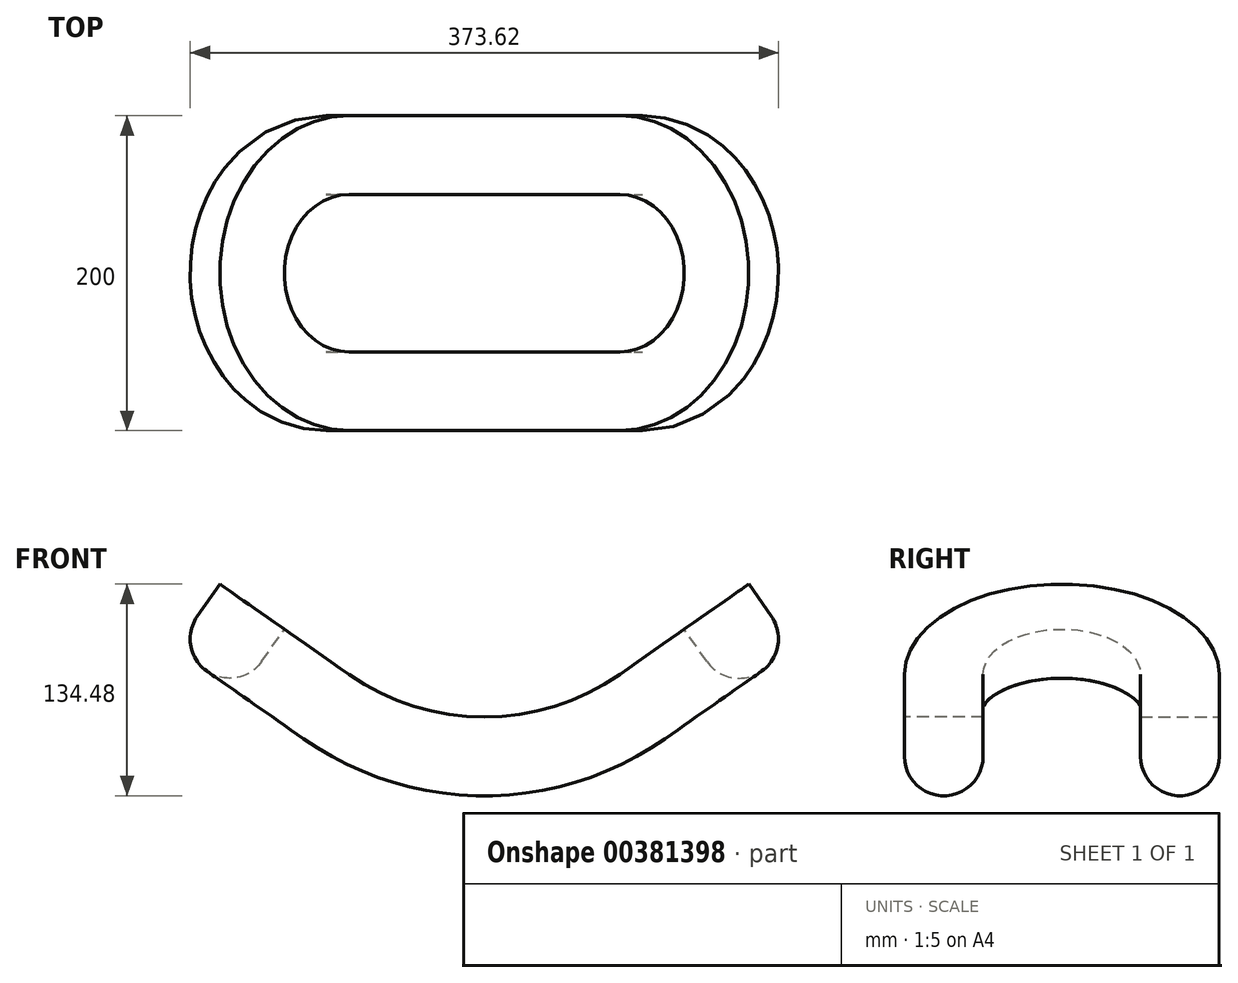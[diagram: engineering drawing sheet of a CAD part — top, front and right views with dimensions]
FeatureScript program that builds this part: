
annotation { "Feature Type Name" : "Feature", "Feature Type Description" : "" }
export const myFeature = defineFeature(function(context is Context, id is Id, definition is map)
    precondition{}
    {
        {
            var Q0;
            Q0=qCreatedBy(makeId("Front.planeOp"),FACE);
            var sketch = newSketch(context, id + "F0", { "sketchPlane" : qUnion([Q0])});
            skArc(sketch, "E0", {"start": v(0, 0) * mm, "mid": v(45.1, 6.94) * mm, "end": v(86.04, 27.13) * mm});
            skLineSegment(sketch, "E1", {"start": v(86.04, 27.13) * mm, "end": v(167.95, 84.48) * mm});
            skLineSegment(sketch, "E2", {"start": v(0, 150) * mm, "end": v(86.04, 27.13) * mm, "construction": true});
            skSolve(sketch);
        }
        {
            var Q0;
            Q0=sQuery(id+"F0.wireOp",EDGE,"E1");
            var Q1;
            Q1=sQuery(id+"F0.wireOp",EDGE,"E0");
            extrude(context, id + "F1", {"bodyType" : ToolBodyType.SURFACE, "surfaceEntities" : qUnion([Q0, Q1]), "depth" : 100 * mm});
        }
        {
            var Q0;
            Q0=makeQuery(id+"F1.opExtrude","SWEPT_FACE",FACE,{"disambiguationData":[OSD([sQuery(id+"F0.wireOp",EDGE,"E1")])]});
            var sketch = newSketch(context, id + "F2", { "sketchPlane" : qUnion([Q0])});
            skArc(sketch, "E3", {"start": v(86.04, 100) * mm, "mid": v(156.75, 70.71) * mm, "end": v(186.04, 0) * mm});
            skSolve(sketch);
        }
        {
            var Q0;
            Q0=qCreatedBy(makeId("Right.planeOp"),FACE);
            var sketch = newSketch(context, id + "F3", { "sketchPlane" : qUnion([Q0])});
            skLineSegment(sketch, "E4.bottom", {"start": v(-50, 0) * mm, "end": v(-100, 0) * mm});
            skLineSegment(sketch, "E4.top", {"start": v(-50, -25) * mm, "end": v(-100, -25) * mm, "construction": true});
            skLineSegment(sketch, "E4.left", {"start": v(-50, 0) * mm, "end": v(-50, -25) * mm});
            skLineSegment(sketch, "E4.right", {"start": v(-100, 0) * mm, "end": v(-100, -25) * mm});
            skArc(sketch, "E5", {"start": v(-50, -25) * mm, "mid": v(-75, -50) * mm, "end": v(-100, -25) * mm});
            skSolve(sketch);
        }
        {
            var Q0;
            Q0=makeQuery(id+"F3.imprint","IMPRINT",FACE,{"disambiguationData":[TD([[makeQuery(id+"F3.imprint","IMPRINT",EDGE,{"derivedFrom":sQuery(id+"F3.wireOp",EDGE,"E4.bottom")}),1.0]])]});
            var Q1;
            Q1=makeQuery(id+"F1.opExtrude","CAP_EDGE",EDGE,{"disambiguationData":[OSD([sQuery(id+"F0.wireOp",EDGE,"E0")])],"isStart":false});
            var Q2;
            Q2=sQuery(id+"F2.wireOp",EDGE,"E3");
            sweep(context, id + "F4", {"profiles" : qUnion([Q0]), "path" : qUnion([Q1, Q2])});
        }
        {
            var Q0;
            Q0=makeQuery(id+"F4.opSweep","SWEPT_BODY",BODY,{"disambiguationData":[OSD([sQuery(id+"F2.wireOp",EDGE,"E3"),sQuery(id+"F3.wireOp",EDGE,"E4.bottom"),sQuery(id+"F3.wireOp",EDGE,"E4.left"),sQuery(id+"F3.wireOp",EDGE,"E4.right"),sQuery(id+"F3.wireOp",EDGE,"E5")])]});
            var Q1;
            Q1=qCreatedBy(makeId("Right.planeOp"),FACE);
            mirror(context, id + "F5", {"operationType" : NewBodyOperationType.ADD, "entities" : qUnion([Q0]), "mirrorPlane" : qUnion([Q1])});
        }
        {
            var Q0;
            Q0=makeQuery(id+"F4.opSweep","SWEPT_BODY",BODY,{"disambiguationData":[OSD([sQuery(id+"F2.wireOp",EDGE,"E3"),sQuery(id+"F3.wireOp",EDGE,"E4.bottom"),sQuery(id+"F3.wireOp",EDGE,"E4.left"),sQuery(id+"F3.wireOp",EDGE,"E4.right"),sQuery(id+"F3.wireOp",EDGE,"E5")])]});
            var Q1;
            Q1=qCreatedBy(makeId("Front.planeOp"),FACE);
            mirror(context, id + "F6", {"operationType" : NewBodyOperationType.ADD, "entities" : qUnion([Q0]), "mirrorPlane" : qUnion([Q1])});
        }
    });
